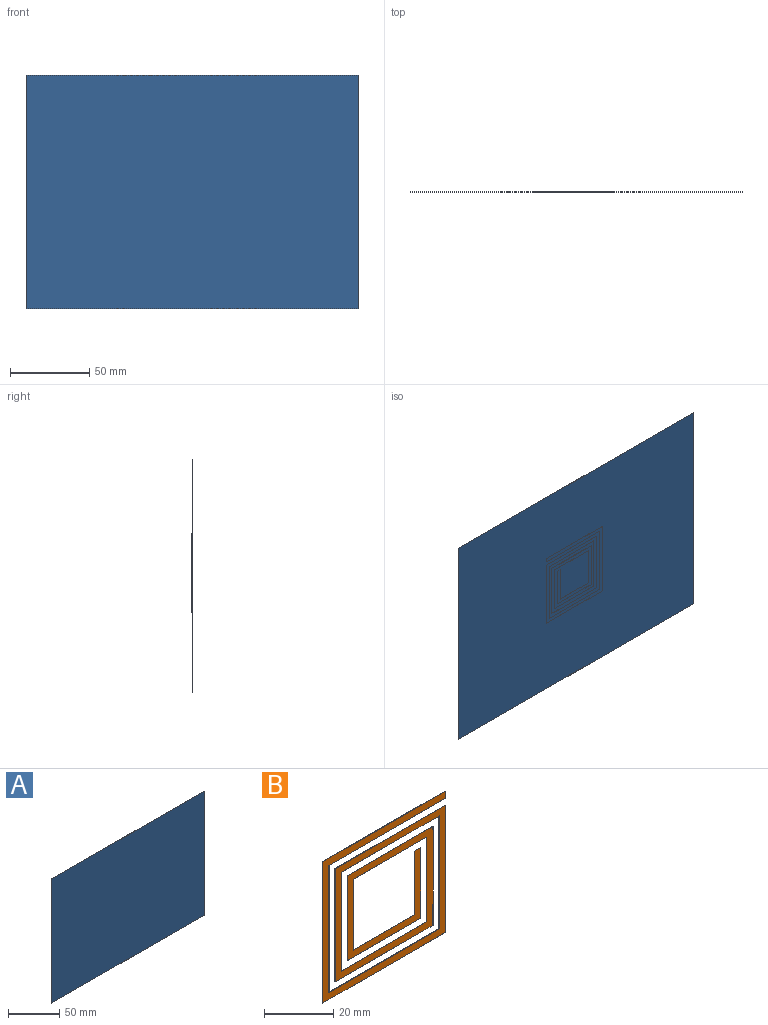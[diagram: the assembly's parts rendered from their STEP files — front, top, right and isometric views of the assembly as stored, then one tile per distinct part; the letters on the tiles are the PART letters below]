
ASSEMBLY  parts=2 mates=1
PART A: 6 faces, bbox 210x0.1x148 mm
  f0: plane 210x0.05mm, normal (0,0,1), area 10.5mm2, adj f1,f3,f4,f5
  f1: plane 148x0.05mm, normal (-1,0,0), area 7.4mm2, adj f0,f2,f4,f5
  f2: plane 210x0.05mm, normal (0,0,-1), area 10.5mm2, adj f1,f3,f4,f5
  f3: plane 148x0.05mm, normal (1,0,0), area 7.4mm2, adj f0,f2,f4,f5
  f4: plane 210x148mm, normal (0,-1,0), area 31080mm2, adj f0,f1,f2,f3
  f5: plane 210x148mm, normal (0,1,0), area 31080mm2, adj f0,f1,f2,f3
PART B: 28 faces, bbox 50x0.1x50 mm
  f0: plane 50x0.09mm, normal (-1,0,0), area 4.3mm2, adj f1,f25,f26,f27
  f1: plane 50x0.09mm, normal (0,0,-1), area 4.3mm2, adj f0,f2,f26,f27
  f2: plane 45x0.09mm, normal (1,0,0), area 3.8mm2, adj f1,f3,f26,f27
  f3: plane 45x0.09mm, normal (0,0,1), area 3.8mm2, adj f2,f4,f26,f27
  f4: plane 40x0.09mm, normal (-1,0,0), area 3.4mm2, adj f3,f5,f26,f27
  f5: plane 40x0.09mm, normal (0,0,-1), area 3.4mm2, adj f4,f6,f26,f27
  f6: plane 35x0.09mm, normal (1,0,0), area 3mm2, adj f5,f7,f26,f27
  f7: plane 35x0.09mm, normal (0,0,1), area 3mm2, adj f6,f8,f26,f27
  f8: plane 30x0.09mm, normal (-1,0,0), area 2.5mm2, adj f7,f9,f26,f27
  f9: plane 30x0.09mm, normal (0,0,-1), area 2.5mm2, adj f8,f10,f26,f27
  f10: plane 25x0.09mm, normal (1,0,0), area 2.1mm2, adj f9,f11,f26,f27
  f11: plane 2.5x0.09mm, normal (0,0,1), area 0.2mm2, adj f10,f12,f26,f27
  f12: plane 22.5x0.09mm, normal (-1,0,0), area 1.9mm2, adj f11,f13,f26,f27
  f13: plane 25x0.09mm, normal (0,0,1), area 2.1mm2, adj f12,f14,f26,f27
  f14: plane 25x0.09mm, normal (1,0,0), area 2.1mm2, adj f13,f15,f26,f27
  f15: plane 30x0.09mm, normal (0,0,-1), area 2.5mm2, adj f14,f16,f26,f27
  f16: plane 30x0.09mm, normal (-1,0,0), area 2.5mm2, adj f15,f17,f26,f27
  f17: plane 35x0.09mm, normal (0,0,1), area 3mm2, adj f16,f18,f26,f27
  f18: plane 35x0.09mm, normal (1,0,0), area 3mm2, adj f17,f19,f26,f27
  f19: plane 40x0.09mm, normal (0,0,-1), area 3.4mm2, adj f18,f20,f26,f27
  f20: plane 40x0.09mm, normal (-1,0,0), area 3.4mm2, adj f19,f21,f26,f27
  f21: plane 45x0.09mm, normal (0,0,1), area 3.8mm2, adj f20,f22,f26,f27
  f22: plane 45x0.09mm, normal (1,0,0), area 3.8mm2, adj f21,f23,f26,f27
  f23: plane 47.5x0.09mm, normal (0,0,-1), area 4mm2, adj f22,f24,f26,f27
  f24: plane 2.5x0.09mm, normal (1,0,0), area 0.2mm2, adj f23,f25,f26,f27
  f25: plane 50x0.09mm, normal (0,0,1), area 4.3mm2, adj f0,f24,f26,f27
  f26: plane 50x50mm, normal (0,-1,0), area 1118.7mm2, adj f0,f1,f2,f3,f4,f5,f6,f7
  f27: plane 50x50mm, normal (0,1,0), area 1118.8mm2, adj f0,f1,f2,f3,f4,f5,f6,f7
PLACE A t=(-32.49,9.01,7.73)mm
PLACE B rot(axis=(0,0,1),180deg) t=(-58.95,9.01,-15.64)mm
MATE planar B.f27 <-> A.f5  axis (0,-1,0) through (-33.84,9.01,9.26)mm
